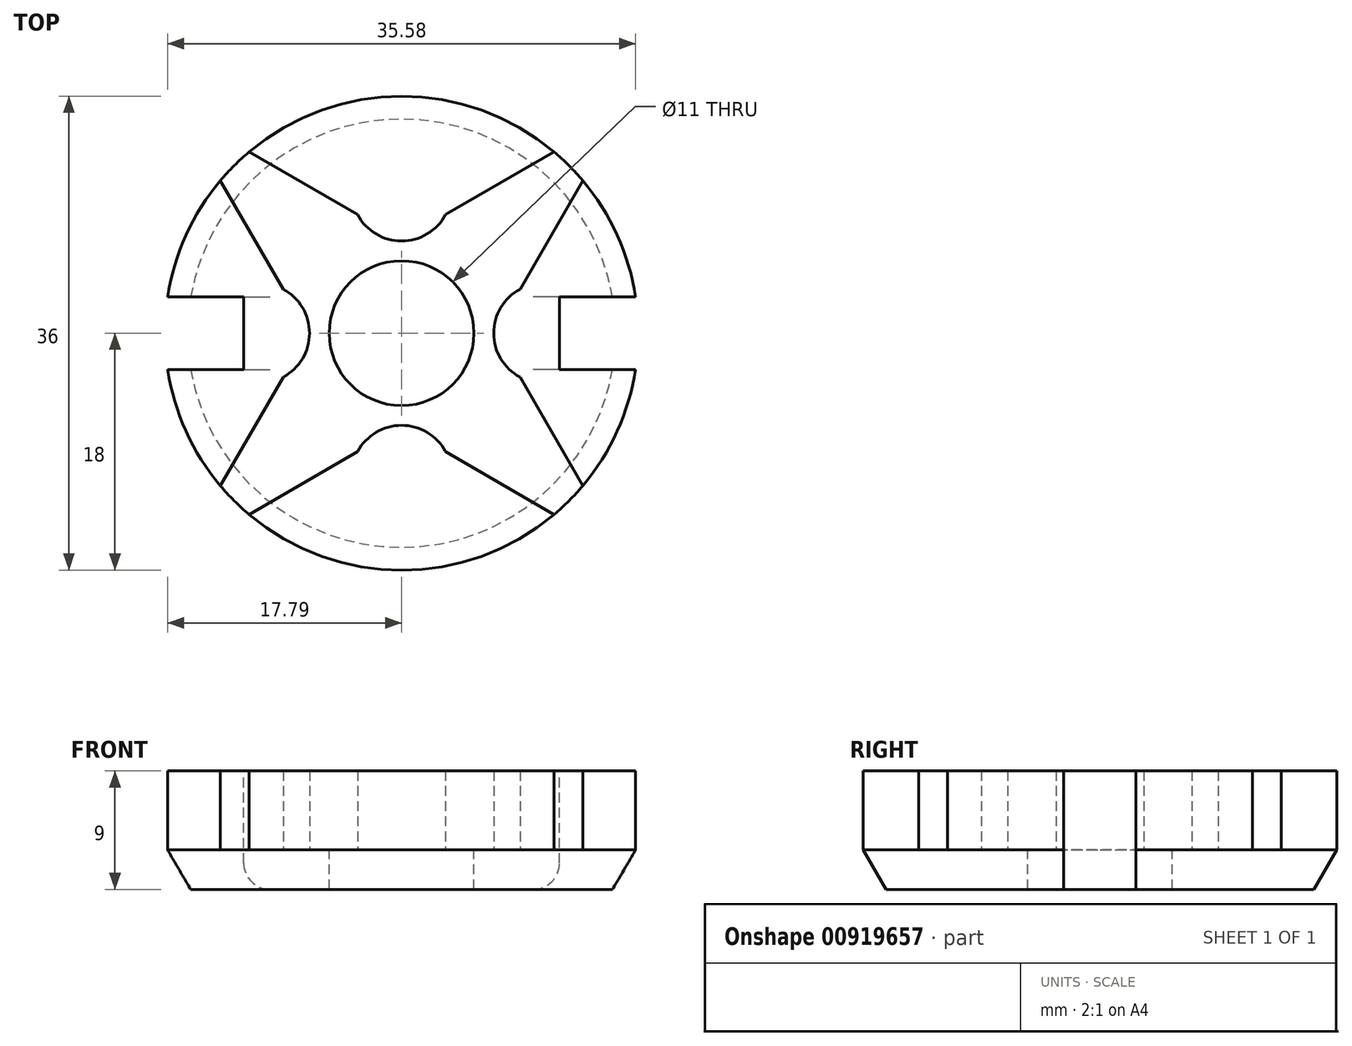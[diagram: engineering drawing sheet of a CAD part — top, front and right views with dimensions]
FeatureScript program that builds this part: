
annotation { "Feature Type Name" : "Feature", "Feature Type Description" : "" }
export const myFeature = defineFeature(function(context is Context, id is Id, definition is map)
    precondition{}
    {
        {
            var Q0;
            Q0=qCreatedBy(makeId("Top.planeOp"),FACE);
            var sketch = newSketch(context, id + "F0", { "sketchPlane" : qUnion([Q0])});
            skCircle(sketch, "E0", {"center": v(0, 0) * mm, "radius": 18 * mm});
            skSolve(sketch);
        }
        {
            var Q0;
            Q0=makeQuery(id+"F0.imprint","IMPRINT",FACE,{"disambiguationData":[TD([[makeQuery(id+"F0.imprint","IMPRINT",EDGE,{"derivedFrom":sQuery(id+"F0.wireOp",EDGE,"E0")}),1.0]])]});
            extrude(context, id + "F1", {"entities" : qUnion([Q0]), "depth" : 6 * mm, "offsetDistance" : 25 * mm, "hasSecondDirection" : true, "secondDirectionOppositeDirection" : true, "secondDirectionDepth" : 3 * mm, "hasSecondDirectionDraft" : true, "secondDirectionDraftAngle" : 30 * degree, "secondDirectionDraftPullDirection" : true});
        }
        {
            var Q0;
            Q0=qCreatedBy(makeId("Top.planeOp"),FACE);
            var sketch = newSketch(context, id + "F2", { "sketchPlane" : qUnion([Q0])});
            skLineSegment(sketch, "E1", {"start": v(-12.57, 14.35) * mm, "end": v(-3.34, 9) * mm});
            skLineSegment(sketch, "E2.MirrorCS", {"start": v(-14.35, 12.57) * mm, "end": v(-9, 3.34) * mm});
            skArc(sketch, "E3", {"start": v(-12.57, 14.35) * mm, "mid": v(-14.14, 14.14) * mm, "end": v(-14.35, 12.57) * mm});
            skLineSegment(sketch, "E4.1.0", {"start": v(-14.35, -12.57) * mm, "end": v(-9, -3.34) * mm});
            skLineSegment(sketch, "E4.1.1", {"start": v(-12.57, -14.35) * mm, "end": v(-3.34, -9) * mm});
            skArc(sketch, "E4.1.2", {"start": v(-14.35, -12.57) * mm, "mid": v(-14.14, -14.14) * mm, "end": v(-12.57, -14.35) * mm});
            skLineSegment(sketch, "E4.2.0", {"start": v(12.57, -14.35) * mm, "end": v(3.34, -9) * mm});
            skLineSegment(sketch, "E4.2.1", {"start": v(14.35, -12.57) * mm, "end": v(9, -3.34) * mm});
            skArc(sketch, "E4.2.2", {"start": v(12.57, -14.35) * mm, "mid": v(14.14, -14.14) * mm, "end": v(14.35, -12.57) * mm});
            skLineSegment(sketch, "E4.3.0", {"start": v(14.35, 12.57) * mm, "end": v(9, 3.34) * mm});
            skLineSegment(sketch, "E4.3.1", {"start": v(12.57, 14.35) * mm, "end": v(3.34, 9) * mm});
            skArc(sketch, "E4.3.2", {"start": v(14.35, 12.57) * mm, "mid": v(14.14, 14.14) * mm, "end": v(12.57, 14.35) * mm});
            skPoint(sketch, "E4.center", {"position": v(0, 0) * mm});
            skArc(sketch, "E5", {"start": v(-3.34, 9) * mm, "mid": v(0, 7) * mm, "end": v(3.34, 9) * mm});
            skArc(sketch, "E6", {"start": v(9, 3.34) * mm, "mid": v(7, 0) * mm, "end": v(9, -3.34) * mm});
            skArc(sketch, "E7", {"start": v(3.34, -9) * mm, "mid": v(0, -7) * mm, "end": v(-3.34, -9) * mm});
            skArc(sketch, "E8", {"start": v(-9, -3.34) * mm, "mid": v(-7, 0) * mm, "end": v(-9, 3.34) * mm});
            skSolve(sketch);
        }
        {
            var Q0;
            Q0=makeQuery(id+"F2.imprint","IMPRINT",FACE,{"disambiguationData":[TD([[makeQuery(id+"F2.imprint","IMPRINT",EDGE,{"derivedFrom":sQuery(id+"F2.wireOp",EDGE,"E1")}),-1.0]])]});
            extrude(context, id + "F3", {"entities" : qUnion([Q0]), "operationType" : NewBodyOperationType.REMOVE, "endBound" : BoundingType.THROUGH_ALL, "depth" : 10 * mm, "offsetDistance" : 25 * mm});
        }
        {
            var Q0;
            Q0=qCreatedBy(makeId("Top.planeOp"),FACE);
            var sketch = newSketch(context, id + "F4", { "sketchPlane" : qUnion([Q0])});
            skCircle(sketch, "E9", {"center": v(0, 0) * mm, "radius": 5 * mm});
            skSolve(sketch);
        }
        {
            var Q0;
            Q0=sQuery(id+"F4.wireOp",VERTEX,"E9.center");
            var Q1;
            Q1=makeQuery(id+"F1.*.split.splitOp","SPLIT",BODY,{"derivedFrom":makeQuery(id+"F1.opExtrude","SWEPT_BODY",BODY,{"disambiguationData":[OSD([sQuery(id+"F0.wireOp",EDGE,"E0")])]})});
            hole(context, id + "F5", {"style" : HoleStyle.SIMPLE, "endStyle" : HoleEndStyle.THROUGH, "standardTappedOrClearance" : lookupTablePath({ "fit" : "Normal", "standard" : "ISO", "size" : "M10", "type" : "Clearance" }), "standardBlindInLast" : lookupTablePath({ "fit" : "Normal", "standard" : "ISO", "engagement" : "75%", "pitch" : "1.5 mm", "size" : "M10", "type" : "Clearance & tapped" }), "holeDiameter" : 11 * mm, "majorDiameter" : 5 * mm, "isTappedThrough" : true, "tappedDepth" : 12 * mm, "tapClearance" : 3, "locations" : qUnion([Q0]), "scope" : qUnion([Q1])});
        }
        {
            var Q0;
            Q0=qCreatedBy(makeId("Top.planeOp"),FACE);
            var sketch = newSketch(context, id + "F6", { "sketchPlane" : qUnion([Q0])});
            skLineSegment(sketch, "E10.bottom", {"start": v(-32, 2.75) * mm, "end": v(-12, 2.75) * mm});
            skLineSegment(sketch, "E10.top", {"start": v(-32, -2.75) * mm, "end": v(-12, -2.75) * mm});
            skLineSegment(sketch, "E10.left", {"start": v(-32, 2.75) * mm, "end": v(-32, -2.75) * mm});
            skLineSegment(sketch, "E10.right", {"start": v(-12, 2.75) * mm, "end": v(-12, -2.75) * mm});
            skLineSegment(sketch, "E11.MirrorCS", {"start": v(12, 2.75) * mm, "end": v(12, -2.75) * mm});
            skLineSegment(sketch, "E12.MirrorCS", {"start": v(32, 2.75) * mm, "end": v(32, -2.75) * mm});
            skLineSegment(sketch, "E13.MirrorCS", {"start": v(32, 2.75) * mm, "end": v(12, 2.75) * mm});
            skLineSegment(sketch, "E14.MirrorCS", {"start": v(32, -2.75) * mm, "end": v(12, -2.75) * mm});
            skSolve(sketch);
        }
        {
            var Q0;
            Q0 = qSketchRegion(id + "F6", true);
            extrude(context, id + "F7", {"entities" : qUnion([Q0]), "operationType" : NewBodyOperationType.REMOVE, "endBound" : BoundingType.SYMMETRIC, "oppositeDirection" : true, "depth" : 25 * mm, "offsetDistance" : 25 * mm});
        }
        {
            var Q0;
            Q0=makeQuery(id+"F7.boolean.opBoolean","INTERSECT",EDGE,{"derivedFrom":[makeQuery(id+"F1.opExtrude","CAP_FACE",FACE,{"disambiguationData":[OSD([sQuery(id+"F0.wireOp",EDGE,"E0")])],"isStart":true}),makeQuery(id+"F7.opExtrude","SWEPT_FACE",FACE,{"disambiguationData":[OSD([sQuery(id+"F6.wireOp",EDGE,"E10.right")])]})]});
            var Q1;
            Q1=makeQuery(id+"F7.boolean.opBoolean","INTERSECT",EDGE,{"derivedFrom":[makeQuery(id+"F1.opExtrude","CAP_FACE",FACE,{"disambiguationData":[OSD([sQuery(id+"F0.wireOp",EDGE,"E0")])],"isStart":true}),makeQuery(id+"F7.opExtrude","SWEPT_FACE",FACE,{"disambiguationData":[OSD([sQuery(id+"F6.wireOp",EDGE,"E11.MirrorCS")])]})]});
            fillet(context, id + "F8", {"entities" : qUnion([Q0, Q1]), "radius" : 2 * mm, "tangentPropagation" : true, "allowEdgeOverflow" : false});
        }
    });
